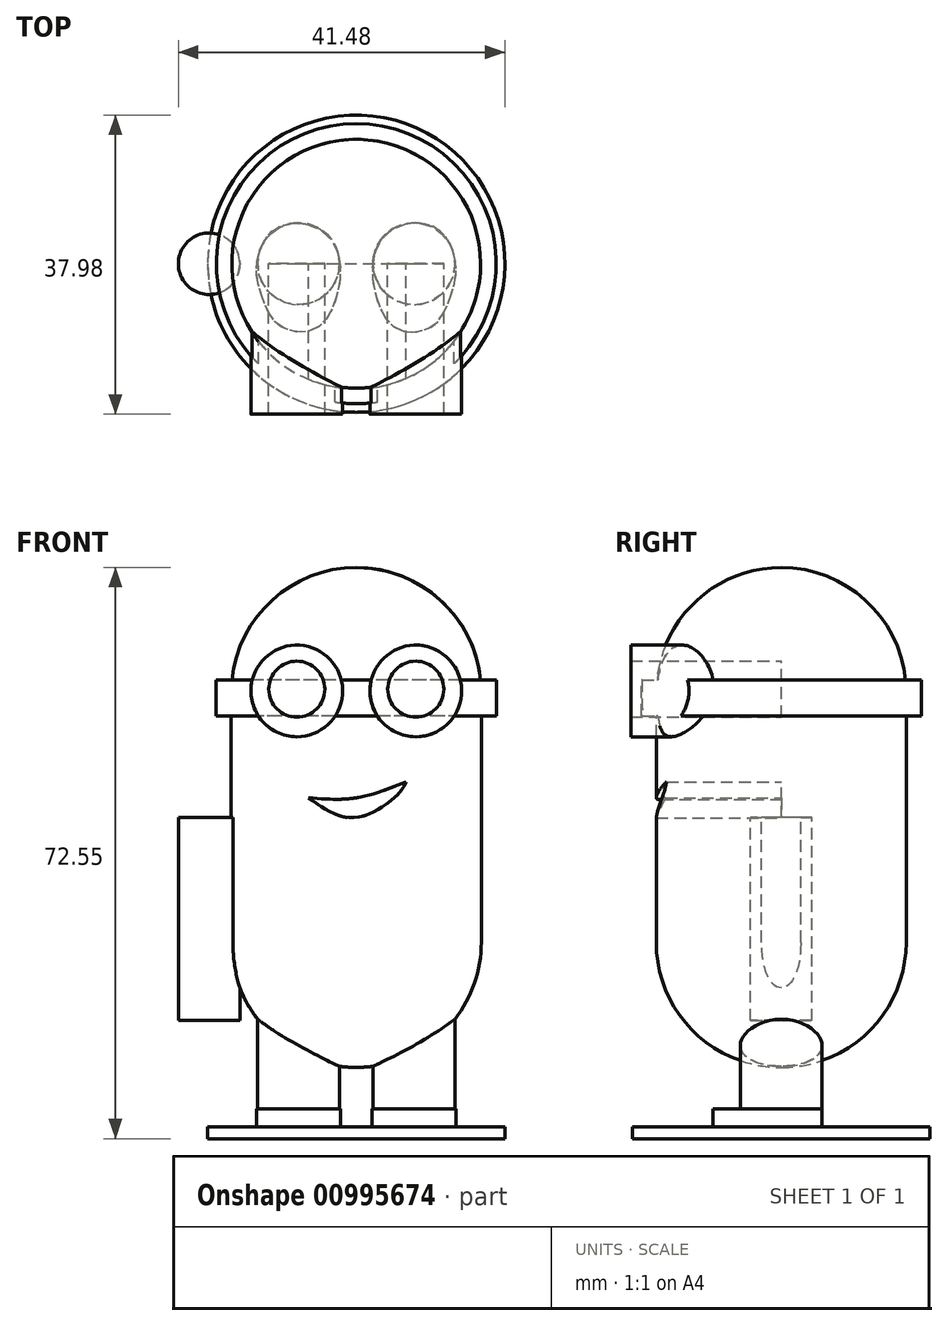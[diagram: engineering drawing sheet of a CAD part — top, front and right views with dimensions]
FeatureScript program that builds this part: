
annotation { "Feature Type Name" : "Feature", "Feature Type Description" : "" }
export const myFeature = defineFeature(function(context is Context, id is Id, definition is map)
    precondition{}
    {
        {
            var Q0;
            Q0=qCreatedBy(makeId("Front.planeOp"),FACE);
            var sketch = newSketch(context, id + "F0", { "sketchPlane" : qUnion([Q0])});
            skLineSegment(sketch, "E0.bottom", {"start": v(0, -15.88) * mm, "end": v(-15.88, -15.88) * mm});
            skLineSegment(sketch, "E0.right", {"start": v(-15.88, -15.88) * mm, "end": v(-15.88, 15.87) * mm});
            skPoint(sketch, "E0.middle", {"position": v(0, 0) * mm});
            skArc(sketch, "E1", {"start": v(0, 31.75) * mm, "mid": v(-11.23, 27.1) * mm, "end": v(-15.88, 15.87) * mm});
            skArc(sketch, "E2", {"start": v(-15.88, -15.88) * mm, "mid": v(-11.23, -27.1) * mm, "end": v(0, -31.75) * mm});
            skLineSegment(sketch, "E3", {"start": v(0, 31.75) * mm, "end": v(0, -31.75) * mm});
            skPoint(sketch, "E0.left.end.orphan", {"position": v(15.88, 15.88) * mm});
            skPoint(sketch, "E4.orphan", {"position": v(15.88, -15.87) * mm});
            skSolve(sketch);
        }
        {
            var Q0;
            {var subQ0=sQuery(id+"F0.wireOp",EDGE,"E0.bottom");Q0=makeQuery(id+"F0.imprint","IMPRINT",FACE,{"disambiguationData":[TD([[makeQuery(id+"F0.imprint","IMPRINT",EDGE,{"derivedFrom":subQ0}),-1.0]])]});}
            var Q1;
            {var subQ0=sQuery(id+"F0.wireOp",EDGE,"E0.bottom");Q1=makeQuery(id+"F0.imprint","IMPRINT",FACE,{"disambiguationData":[TD([[makeQuery(id+"F0.imprint","IMPRINT",EDGE,{"derivedFrom":subQ0}),1.0]])]});}
            var Q2;
            Q2=sQuery(id+"F0.wireOp",EDGE,"E3");
            revolve(context, id + "F1", {"surfaceOperationType" : NewSurfaceOperationType.NEW, "entities" : qUnion([Q0, Q1]), "axis" : qUnion([Q2]), "revolveType" : RevolveType.FULL});
        }
        {
            var Q0;
            Q0=qCreatedBy(makeId("Front.planeOp"),FACE);
            var sketch = newSketch(context, id + "F2", { "sketchPlane" : qUnion([Q0])});
            skLineSegment(sketch, "E5", {"start": v(0, 22.67) * mm, "end": v(0, -11.42) * mm, "construction": true});
            skCircle(sketch, "E6", {"center": v(-7.33, 15.85) * mm, "radius": 5.37 * mm});
            skCircle(sketch, "E7", {"center": v(-7.33, 15.85) * mm, "radius": 3.16 * mm});
            skCircle(sketch, "E8.MirrorC", {"center": v(7.33, 15.85) * mm, "radius": 3.16 * mm});
            skCircle(sketch, "E9.MirrorC", {"center": v(7.33, 15.85) * mm, "radius": 5.37 * mm});
            skSolve(sketch);
        }
        {
            var Q0;
            Q0=qCreatedBy(makeId("Front.planeOp"),FACE);
            var sketch = newSketch(context, id + "F3", { "sketchPlane" : qUnion([Q0])});
            skFitSpline(sketch, "E10", {"points": [v(-6.05, 2.5) * mm, v(0, 0) * mm, v(5.59, 3.3) * mm, v(6.3, 4.54) * mm], "startDerivative": vector(14.25, -10.21) * mm, "endDerivative": vector(2.03, 5.64) * mm});
            skFitSpline(sketch, "E11", {"points": [v(-6.05, 2.5) * mm, v(0, 2.5) * mm, v(6.3, 4.54) * mm], "startDerivative": vector(12.39, -0.98) * mm, "endDerivative": vector(12.3, 5.02) * mm});
            skSolve(sketch);
        }
        {
            var Q0;
            Q0 = qSketchRegion(id + "F3", true);
            extrude(context, id + "F4", {"entities" : qUnion([Q0]), "operationType" : NewBodyOperationType.REMOVE, "depth" : 28.2 * mm, "offsetDistance" : 25 * mm});
        }
        {
            var Q0;
            Q0=qCreatedBy(makeId("Top.planeOp"),FACE);
            var sketch = newSketch(context, id + "F5", { "sketchPlane" : qUnion([Q0])});
            skCircle(sketch, "E12", {"center": v(-18.7, 0) * mm, "radius": 3.9 * mm});
            skLineSegment(sketch, "E13", {"start": v(0, 10.63) * mm, "end": v(0, -9.15) * mm, "construction": true});
            skCircle(sketch, "E14.MirrorC", {"center": v(18.7, 0) * mm, "radius": 3.9 * mm});
            skSolve(sketch);
        }
        {
            var Q0;
            Q0=makeQuery(id+"F5.imprint","IMPRINT",FACE,{"disambiguationData":[TD([[makeQuery(id+"F5.imprint","IMPRINT",EDGE,{"derivedFrom":sQuery(id+"F5.wireOp",EDGE,"E14.MirrorC")}),-1.0]])]});
            var Q1;
            Q1=makeQuery(id+"F5.imprint","IMPRINT",FACE,{"disambiguationData":[TD([[makeQuery(id+"F5.imprint","IMPRINT",EDGE,{"derivedFrom":sQuery(id+"F5.wireOp",EDGE,"E12")}),1.0]])]});
            extrude(context, id + "F6", {"entities" : qUnion([Q0, Q1]), "operationType" : NewBodyOperationType.ADD, "oppositeDirection" : true, "depth" : 25.8 * mm, "offsetDistance" : 25 * mm});
        }
        {
            var Q0;
            Q0=qCreatedBy(makeId("Top.planeOp"),FACE);
            var sketch = newSketch(context, id + "F7", { "sketchPlane" : qUnion([Q0])});
            skLineSegment(sketch, "E15", {"start": v(0, 11.08) * mm, "end": v(0, -10.06) * mm, "construction": true});
            skCircle(sketch, "E16", {"center": v(-7.33, 0) * mm, "radius": 5.2 * mm});
            skCircle(sketch, "E17.MirrorC", {"center": v(7.33, 0) * mm, "radius": 5.2 * mm});
            skSolve(sketch);
        }
        {
            var Q0;
            Q0 = qSketchRegion(id + "F7", true);
            extrude(context, id + "F8", {"entities" : qUnion([Q0]), "operationType" : NewBodyOperationType.ADD, "oppositeDirection" : true, "depth" : 37 * mm, "offsetDistance" : 25 * mm});
        }
        {
            var Q0;
            Q0=makeQuery(id+"F8.opExtrude","CAP_FACE",FACE,{"disambiguationData":[OSD([sQuery(id+"F7.wireOp",EDGE,"E17.MirrorC")])],"isStart":false});
            var sketch = newSketch(context, id + "F9", { "sketchPlane" : qUnion([Q0])});
            skLineSegment(sketch, "E18", {"start": v(0, 6.7) * mm, "end": v(0, -9.8) * mm, "construction": true});
            skFitSpline(sketch, "E19", {"points": [v(-4.46, -4.29) * mm, v(-2.06, 0) * mm, v(-2.97, 5.49) * mm, v(-5.46, 8.38) * mm, v(-9.48, 8.07) * mm, v(-11.75, 4.8) * mm, v(-12.65, 0) * mm, v(-9.98, -4.6) * mm, v(-4.46, -4.29) * mm]});
            skFitSpline(sketch, "E20.MirrorC", {"points": [v(4.46, -4.29) * mm, v(2.06, 0) * mm, v(2.97, 5.49) * mm, v(5.46, 8.38) * mm, v(9.48, 8.07) * mm, v(11.75, 4.8) * mm, v(12.65, 0) * mm, v(9.98, -4.6) * mm, v(4.46, -4.29) * mm]});
            skSolve(sketch);
        }
        {
            var Q0;
            Q0 = qSketchRegion(id + "F9", true);
            extrude(context, id + "F10", {"entities" : qUnion([Q0]), "operationType" : NewBodyOperationType.ADD, "depth" : 2.3 * mm, "offsetDistance" : 25 * mm});
        }
        {
            var Q0;
            Q0=makeQuery(id+"F10.opExtrude","CAP_FACE",FACE,{"disambiguationData":[OSD([sQuery(id+"F9.wireOp",EDGE,"E19")])],"isStart":false});
            var sketch = newSketch(context, id + "F11", { "sketchPlane" : qUnion([Q0])});
            skCircle(sketch, "E21", {"center": v(0, 0) * mm, "radius": 18.88 * mm});
            skSolve(sketch);
        }
        {
            var Q0;
            Q0 = qSketchRegion(id + "F11", true);
            extrude(context, id + "F12", {"entities" : qUnion([Q0]), "operationType" : NewBodyOperationType.ADD, "depth" : 1.5 * mm, "offsetDistance" : 25 * mm});
        }
        {
            var Q0;
            Q0=qCreatedBy(makeId("Front.planeOp"),FACE);
            var sketch = newSketch(context, id + "F13", { "sketchPlane" : qUnion([Q0])});
            skLineSegment(sketch, "E22.bottom", {"start": v(-15.06, 12.9) * mm, "end": v(-17.78, 12.9) * mm});
            skLineSegment(sketch, "E22.top", {"start": v(-15.06, 17.44) * mm, "end": v(-17.78, 17.44) * mm});
            skLineSegment(sketch, "E22.left", {"start": v(-15.06, 12.9) * mm, "end": v(-15.06, 17.44) * mm});
            skLineSegment(sketch, "E22.right", {"start": v(-17.78, 12.9) * mm, "end": v(-17.78, 17.44) * mm});
            skPoint(sketch, "E22.middle", {"position": v(-16.42, 15.17) * mm});
            skLineSegment(sketch, "E23", {"start": v(0, 25.17) * mm, "end": v(0, 6.76) * mm, "construction": true});
            skSolve(sketch);
        }
        {
            var Q0;
            Q0=makeQuery(id+"F13.imprint","IMPRINT",FACE,{"disambiguationData":[TD([[makeQuery(id+"F13.imprint","IMPRINT",EDGE,{"derivedFrom":sQuery(id+"F13.wireOp",EDGE,"E22.bottom")}),-1.0]])]});
            var Q1;
            Q1=sQuery(id+"F13.wireOp",EDGE,"E23");
            revolve(context, id + "F14", {"operationType" : NewBodyOperationType.ADD, "surfaceOperationType" : NewSurfaceOperationType.NEW, "entities" : qUnion([Q0]), "axis" : qUnion([Q1]), "revolveType" : RevolveType.FULL});
        }
        {
            var Q0;
            Q0=qCreatedBy(makeId("Front.planeOp"),FACE);
            var sketch = newSketch(context, id + "F15", { "sketchPlane" : qUnion([Q0])});
            skCircle(sketch, "E24", {"center": v(-7.56, 16.08) * mm, "radius": 5.82 * mm});
            skCircle(sketch, "E25.MirrorC", {"center": v(7.56, 16.08) * mm, "radius": 5.82 * mm});
            skSolve(sketch);
        }
        {
            var Q0;
            Q0 = qSketchRegion(id + "F15", true);
            extrude(context, id + "F16", {"entities" : qUnion([Q0]), "operationType" : NewBodyOperationType.ADD, "depth" : 19.1 * mm, "offsetDistance" : 25 * mm});
        }
        {
            var Q0;
            Q0=qCreatedBy(makeId("Front.planeOp"),FACE);
            var sketch = newSketch(context, id + "F17", { "sketchPlane" : qUnion([Q0])});
            skCircle(sketch, "E26", {"center": v(-7.56, 16.3) * mm, "radius": 3.56 * mm});
            skCircle(sketch, "E27.MirrorC", {"center": v(7.56, 16.3) * mm, "radius": 3.56 * mm});
            skSolve(sketch);
        }
        {
            var Q0;
            Q0 = qSketchRegion(id + "F17", true);
            extrude(context, id + "F18", {"entities" : qUnion([Q0]), "operationType" : NewBodyOperationType.REMOVE, "depth" : 30 * mm, "offsetDistance" : 25 * mm});
        }
    });
